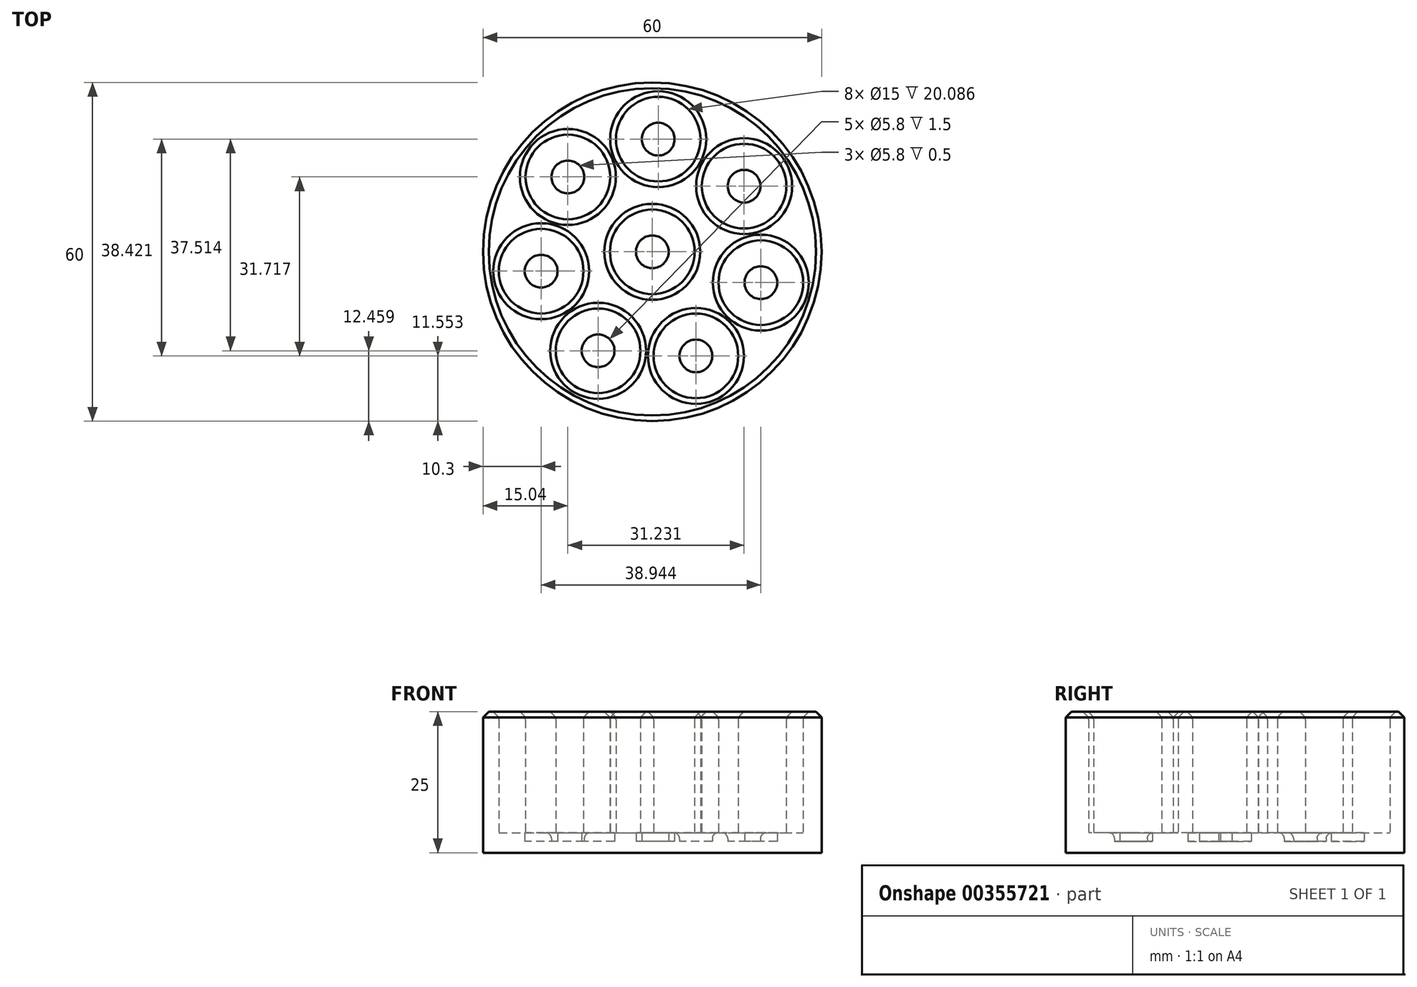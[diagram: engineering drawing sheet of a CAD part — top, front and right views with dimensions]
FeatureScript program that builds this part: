
annotation { "Feature Type Name" : "Feature", "Feature Type Description" : "" }
export const myFeature = defineFeature(function(context is Context, id is Id, definition is map)
    precondition{}
    {
        {
            var Q0;
            Q0=qCreatedBy(makeId("Top.planeOp"),FACE);
            var sketch = newSketch(context, id + "F0", { "sketchPlane" : qUnion([Q0])});
            skCircle(sketch, "E0", {"center": v(0, 0) * mm, "radius": 7.5 * mm});
            skCircle(sketch, "E1.1.0", {"center": v(-4.74, -16.7) * mm, "radius": 7.5 * mm});
            skCircle(sketch, "E1.2.0", {"center": v(5.36, -30.81) * mm, "radius": 7.5 * mm});
            skPoint(sketch, "E1.center", {"position": v(14.96, -13.27) * mm});
            skCircle(sketch, "E2.0.3.0", {"center": v(22.69, -31.72) * mm, "radius": 7.5 * mm});
            skCircle(sketch, "E2.0.4.0", {"center": v(34.2, -18.73) * mm, "radius": 7.5 * mm});
            skCircle(sketch, "E2.0.5.0", {"center": v(31.23, -1.63) * mm, "radius": 7.5 * mm});
            skCircle(sketch, "E2.0.6.0", {"center": v(16, 6.7) * mm, "radius": 7.5 * mm});
            skCircle(sketch, "E3", {"center": v(14.96, -13.27) * mm, "radius": 7.5 * mm});
            skCircle(sketch, "E4", {"center": v(14.96, -13.27) * mm, "radius": 30 * mm});
            skSolve(sketch);
        }
        {
            var Q0;
            Q0 = qSketchRegion(id + "F0", true);
            extrude(context, id + "F1", {"entities" : qUnion([Q0]), "depth" : 25 * mm});
        }
        {
            var Q0;
            Q0=makeQuery(id+"F0.imprint","IMPRINT",FACE,{"disambiguationData":[TD([[makeQuery(id+"F0.imprint","IMPRINT",EDGE,{"derivedFrom":sQuery(id+"F0.wireOp",EDGE,"E2.0.5.0")}),1.0]])]});
            var Q1;
            Q1=makeQuery(id+"F0.imprint","IMPRINT",FACE,{"disambiguationData":[TD([[makeQuery(id+"F0.imprint","IMPRINT",EDGE,{"derivedFrom":sQuery(id+"F0.wireOp",EDGE,"E2.0.4.0")}),1.0]])]});
            var Q2;
            Q2=makeQuery(id+"F0.imprint","IMPRINT",FACE,{"disambiguationData":[TD([[makeQuery(id+"F0.imprint","IMPRINT",EDGE,{"derivedFrom":sQuery(id+"F0.wireOp",EDGE,"E2.0.3.0")}),1.0]])]});
            var Q3;
            Q3=makeQuery(id+"F0.imprint","IMPRINT",FACE,{"disambiguationData":[TD([[makeQuery(id+"F0.imprint","IMPRINT",EDGE,{"derivedFrom":sQuery(id+"F0.wireOp",EDGE,"E3")}),1.0]])]});
            var Q4;
            Q4=makeQuery(id+"F0.imprint","IMPRINT",FACE,{"disambiguationData":[TD([[makeQuery(id+"F0.imprint","IMPRINT",EDGE,{"derivedFrom":sQuery(id+"F0.wireOp",EDGE,"E2.0.6.0")}),1.0]])]});
            var Q5;
            Q5=makeQuery(id+"F0.imprint","IMPRINT",FACE,{"disambiguationData":[TD([[makeQuery(id+"F0.imprint","IMPRINT",EDGE,{"derivedFrom":sQuery(id+"F0.wireOp",EDGE,"E2.0.7.0")}),1.0]])]});
            var Q6;
            Q6=makeQuery(id+"F0.imprint","IMPRINT",FACE,{"disambiguationData":[TD([[makeQuery(id+"F0.imprint","IMPRINT",EDGE,{"derivedFrom":sQuery(id+"F0.wireOp",EDGE,"E0")}),1.0]])]});
            var Q7;
            Q7=makeQuery(id+"F0.imprint","IMPRINT",FACE,{"disambiguationData":[TD([[makeQuery(id+"F0.imprint","IMPRINT",EDGE,{"derivedFrom":sQuery(id+"F0.wireOp",EDGE,"E1.2.0")}),1.0]])]});
            var Q8;
            Q8=makeQuery(id+"F0.imprint","IMPRINT",FACE,{"disambiguationData":[TD([[makeQuery(id+"F0.imprint","IMPRINT",EDGE,{"derivedFrom":sQuery(id+"F0.wireOp",EDGE,"E1.1.0")}),1.0]])]});
            extrude(context, id + "F2", {"entities" : qUnion([Q0, Q1, Q2, Q3, Q4, Q5, Q6, Q7, Q8]), "operationType" : NewBodyOperationType.ADD, "depth" : 2 * mm});
        }
        {
            var Q0;
            Q0=makeQuery(id+"F2.opExtrude","CAP_FACE",FACE,{"disambiguationData":[OSD([sQuery(id+"F0.wireOp",EDGE,"E1.1.0")])],"isStart":false});
            var sketch = newSketch(context, id + "F3", { "sketchPlane" : qUnion([Q0])});
            skPoint(sketch, "E5.0", {"position": v(-4.74, -16.7) * mm});
            skPoint(sketch, "E5.1", {"position": v(5.36, -30.81) * mm});
            skPoint(sketch, "E5.2", {"position": v(22.69, -31.72) * mm});
            skPoint(sketch, "E5.3", {"position": v(34.2, -18.73) * mm});
            skPoint(sketch, "E5.4", {"position": v(31.23, -1.63) * mm});
            skPoint(sketch, "E5.5", {"position": v(16, 6.7) * mm});
            skPoint(sketch, "E5.6", {"position": v(14.45, 7.03) * mm});
            skPoint(sketch, "E5.7", {"position": v(14.96, -13.27) * mm});
            skPoint(sketch, "E5.8", {"position": v(0, 0) * mm});
            skCircle(sketch, "E6", {"center": v(-4.74, -16.7) * mm, "radius": 2.9 * mm});
            skCircle(sketch, "E7", {"center": v(5.36, -30.81) * mm, "radius": 2.9 * mm});
            skCircle(sketch, "E8", {"center": v(22.69, -31.72) * mm, "radius": 2.9 * mm});
            skCircle(sketch, "E9", {"center": v(14.96, -13.27) * mm, "radius": 2.9 * mm});
            skCircle(sketch, "E10", {"center": v(0, 0) * mm, "radius": 2.9 * mm});
            skCircle(sketch, "E11", {"center": v(34.2, -18.73) * mm, "radius": 2.9 * mm});
            skCircle(sketch, "E12", {"center": v(31.23, -1.63) * mm, "radius": 2.9 * mm});
            skCircle(sketch, "E13", {"center": v(16, 6.7) * mm, "radius": 2.9 * mm});
            skCircle(sketch, "E14.0", {"center": v(5.36, -30.81) * mm, "radius": 7.5 * mm});
            skCircle(sketch, "E14.2", {"center": v(14.96, -13.27) * mm, "radius": 7.5 * mm});
            skCircle(sketch, "E14.3", {"center": v(22.69, -31.72) * mm, "radius": 7.5 * mm});
            skCircle(sketch, "E14.4", {"center": v(34.2, -18.73) * mm, "radius": 7.5 * mm});
            skCircle(sketch, "E14.5", {"center": v(31.23, -1.63) * mm, "radius": 7.5 * mm});
            skCircle(sketch, "E14.6", {"center": v(16, 6.7) * mm, "radius": 7.5 * mm});
            skCircle(sketch, "E14.7", {"center": v(-4.74, -16.7) * mm, "radius": 7.5 * mm});
            skCircle(sketch, "E14.8", {"center": v(0, 0) * mm, "radius": 7.5 * mm});
            skSolve(sketch);
        }
        {
            var Q0;
            Q0 = qSketchRegion(id + "F3", true);
            extrude(context, id + "F4", {"entities" : qUnion([Q0]), "operationType" : NewBodyOperationType.ADD, "depth" : 1.5 * mm});
        }
        {
            var Q0;
            Q0=makeQuery(id+"F1.opExtrude","CAP_EDGE",EDGE,{"disambiguationData":[OSD([sQuery(id+"F0.wireOp",EDGE,"E1.1.0")])],"isStart":false});
            var Q1;
            Q1=makeQuery(id+"F1.opExtrude","CAP_EDGE",EDGE,{"disambiguationData":[OSD([sQuery(id+"F0.wireOp",EDGE,"E0")])],"isStart":false});
            var Q2;
            Q2=makeQuery(id+"F1.opExtrude","CAP_EDGE",EDGE,{"disambiguationData":[OSD([sQuery(id+"F0.wireOp",EDGE,"E2.0.7.0")])],"isStart":false});
            var Q3;
            Q3=makeQuery(id+"F1.opExtrude","CAP_EDGE",EDGE,{"disambiguationData":[OSD([sQuery(id+"F0.wireOp",EDGE,"E2.0.6.0")])],"isStart":false});
            var Q4;
            Q4=makeQuery(id+"F1.opExtrude","CAP_EDGE",EDGE,{"disambiguationData":[OSD([sQuery(id+"F0.wireOp",EDGE,"E2.0.5.0")])],"isStart":false});
            var Q5;
            Q5=makeQuery(id+"F1.opExtrude","CAP_EDGE",EDGE,{"disambiguationData":[OSD([sQuery(id+"F0.wireOp",EDGE,"E2.0.4.0")])],"isStart":false});
            var Q6;
            Q6=makeQuery(id+"F1.opExtrude","CAP_EDGE",EDGE,{"disambiguationData":[OSD([sQuery(id+"F0.wireOp",EDGE,"E3")])],"isStart":false});
            var Q7;
            Q7=makeQuery(id+"F1.opExtrude","CAP_EDGE",EDGE,{"disambiguationData":[OSD([sQuery(id+"F0.wireOp",EDGE,"E1.2.0")])],"isStart":false});
            var Q8;
            Q8=makeQuery(id+"F1.opExtrude","CAP_EDGE",EDGE,{"disambiguationData":[OSD([sQuery(id+"F0.wireOp",EDGE,"E2.0.3.0")])],"isStart":false});
            var Q9;
            Q9=makeQuery(id+"F1.opExtrude","CAP_EDGE",EDGE,{"disambiguationData":[OSD([sQuery(id+"F0.wireOp",EDGE,"E4")])],"isStart":false});
            chamfer(context, id + "F5", {"entities" : qUnion([Q0, Q1, Q2, Q3, Q4, Q5, Q6, Q7, Q8, Q9]), "width" : 1 * mm, "tangentPropagation" : true});
        }
        {
            var Q0;
            {var subQ0=sQuery(id+"F0.wireOp",EDGE,"E1.2.0");Q0=makeQuery(id+"F5.opChamfer","BLEND_EDGE",EDGE,{"blendedFrom":[makeQuery(id+"F1.opExtrude","CAP_EDGE",EDGE,{"disambiguationData":[OSD([subQ0])],"isStart":false}),makeQuery(id+"F1.opExtrude","SWEPT_FACE",FACE,{"disambiguationData":[OSD([subQ0])]})],"blendedInto":[makeQuery(id+"F1.opExtrude","SWEPT_FACE",FACE,{"disambiguationData":[OSD([subQ0])]})]});}
            var Q1;
            {var subQ0=sQuery(id+"F0.wireOp",EDGE,"E1.1.0");Q1=makeQuery(id+"F5.opChamfer","BLEND_EDGE",EDGE,{"blendedFrom":[makeQuery(id+"F1.opExtrude","CAP_EDGE",EDGE,{"disambiguationData":[OSD([subQ0])],"isStart":false}),makeQuery(id+"F1.opExtrude","SWEPT_FACE",FACE,{"disambiguationData":[OSD([subQ0])]})],"blendedInto":[makeQuery(id+"F1.opExtrude","SWEPT_FACE",FACE,{"disambiguationData":[OSD([subQ0])]})]});}
            var Q2;
            {var subQ0=sQuery(id+"F0.wireOp",EDGE,"E2.0.3.0");Q2=makeQuery(id+"F5.opChamfer","BLEND_EDGE",EDGE,{"blendedFrom":[makeQuery(id+"F1.opExtrude","CAP_EDGE",EDGE,{"disambiguationData":[OSD([subQ0])],"isStart":false}),makeQuery(id+"F1.opExtrude","SWEPT_FACE",FACE,{"disambiguationData":[OSD([subQ0])]})],"blendedInto":[makeQuery(id+"F1.opExtrude","SWEPT_FACE",FACE,{"disambiguationData":[OSD([subQ0])]})]});}
            var Q3;
            {var subQ0=sQuery(id+"F0.wireOp",EDGE,"E2.0.4.0");Q3=makeQuery(id+"F5.opChamfer","BLEND_EDGE",EDGE,{"blendedFrom":[makeQuery(id+"F1.opExtrude","CAP_EDGE",EDGE,{"disambiguationData":[OSD([subQ0])],"isStart":false}),makeQuery(id+"F1.opExtrude","SWEPT_FACE",FACE,{"disambiguationData":[OSD([subQ0])]})],"blendedInto":[makeQuery(id+"F1.opExtrude","SWEPT_FACE",FACE,{"disambiguationData":[OSD([subQ0])]})]});}
            var Q4;
            {var subQ0=sQuery(id+"F0.wireOp",EDGE,"E2.0.5.0");Q4=makeQuery(id+"F5.opChamfer","BLEND_EDGE",EDGE,{"blendedFrom":[makeQuery(id+"F1.opExtrude","CAP_EDGE",EDGE,{"disambiguationData":[OSD([subQ0])],"isStart":false}),makeQuery(id+"F1.opExtrude","SWEPT_FACE",FACE,{"disambiguationData":[OSD([subQ0])]})],"blendedInto":[makeQuery(id+"F1.opExtrude","SWEPT_FACE",FACE,{"disambiguationData":[OSD([subQ0])]})]});}
            var Q5;
            {var subQ0=sQuery(id+"F0.wireOp",EDGE,"E2.0.6.0");Q5=makeQuery(id+"F5.opChamfer","BLEND_EDGE",EDGE,{"blendedFrom":[makeQuery(id+"F1.opExtrude","CAP_EDGE",EDGE,{"disambiguationData":[OSD([subQ0])],"isStart":false}),makeQuery(id+"F1.opExtrude","SWEPT_FACE",FACE,{"disambiguationData":[OSD([subQ0])]})],"blendedInto":[makeQuery(id+"F1.opExtrude","SWEPT_FACE",FACE,{"disambiguationData":[OSD([subQ0])]})]});}
            var Q6;
            {var subQ0=sQuery(id+"F0.wireOp",EDGE,"E0");Q6=makeQuery(id+"F5.opChamfer","BLEND_EDGE",EDGE,{"blendedFrom":[makeQuery(id+"F1.opExtrude","CAP_EDGE",EDGE,{"disambiguationData":[OSD([subQ0])],"isStart":false}),makeQuery(id+"F1.opExtrude","SWEPT_FACE",FACE,{"disambiguationData":[OSD([subQ0])]})],"blendedInto":[makeQuery(id+"F1.opExtrude","SWEPT_FACE",FACE,{"disambiguationData":[OSD([subQ0])]})]});}
            var Q7;
            {var subQ0=sQuery(id+"F0.wireOp",EDGE,"E3");Q7=makeQuery(id+"F5.opChamfer","BLEND_EDGE",EDGE,{"blendedFrom":[makeQuery(id+"F1.opExtrude","CAP_EDGE",EDGE,{"disambiguationData":[OSD([subQ0])],"isStart":false}),makeQuery(id+"F1.opExtrude","SWEPT_FACE",FACE,{"disambiguationData":[OSD([subQ0])]})],"blendedInto":[makeQuery(id+"F1.opExtrude","SWEPT_FACE",FACE,{"disambiguationData":[OSD([subQ0])]})]});}
            var Q8;
            Q8=makeQuery(id+"F4.opExtrude","CAP_EDGE",EDGE,{"disambiguationData":[OSD([sQuery(id+"F3.wireOp",EDGE,"E7")])],"isStart":true});
            var Q9;
            Q9=makeQuery(id+"F4.opExtrude","CAP_EDGE",EDGE,{"disambiguationData":[OSD([sQuery(id+"F3.wireOp",EDGE,"E6")])],"isStart":true});
            var Q10;
            Q10=makeQuery(id+"F4.opExtrude","CAP_EDGE",EDGE,{"disambiguationData":[OSD([sQuery(id+"F3.wireOp",EDGE,"E10")])],"isStart":false});
            var Q11;
            Q11=makeQuery(id+"F4.opExtrude","CAP_EDGE",EDGE,{"disambiguationData":[OSD([sQuery(id+"F3.wireOp",EDGE,"Eor7ybkG-s9XB-PS9b-kSbm-frpLWbX5gBem")])],"isStart":true});
            var Q12;
            Q12=makeQuery(id+"F4.opExtrude","CAP_EDGE",EDGE,{"disambiguationData":[OSD([sQuery(id+"F3.wireOp",EDGE,"E9")])],"isStart":true});
            var Q13;
            Q13=makeQuery(id+"F4.opExtrude","CAP_EDGE",EDGE,{"disambiguationData":[OSD([sQuery(id+"F3.wireOp",EDGE,"E8")])],"isStart":false});
            var Q14;
            Q14=makeQuery(id+"F4.opExtrude","CAP_EDGE",EDGE,{"disambiguationData":[OSD([sQuery(id+"F3.wireOp",EDGE,"E11")])],"isStart":true});
            var Q15;
            Q15=makeQuery(id+"F4.opExtrude","CAP_EDGE",EDGE,{"disambiguationData":[OSD([sQuery(id+"F3.wireOp",EDGE,"E12")])],"isStart":false});
            var Q16;
            Q16=makeQuery(id+"F4.opExtrude","CAP_EDGE",EDGE,{"disambiguationData":[OSD([sQuery(id+"F3.wireOp",EDGE,"E13")])],"isStart":true});
            var Q17;
            Q17=makeQuery(id+"F4.opExtrude","CAP_EDGE",EDGE,{"disambiguationData":[OSD([sQuery(id+"F3.wireOp",EDGE,"E14.6")])],"isStart":false});
            var Q18;
            Q18=makeQuery(id+"F4.opExtrude","CAP_EDGE",EDGE,{"disambiguationData":[OSD([sQuery(id+"F3.wireOp",EDGE,"E14.2")])],"isStart":false});
            var Q19;
            Q19=makeQuery(id+"F4.opExtrude","CAP_EDGE",EDGE,{"disambiguationData":[OSD([sQuery(id+"F3.wireOp",EDGE,"E14.1")])],"isStart":false});
            var Q20;
            Q20=makeQuery(id+"F4.opExtrude","CAP_EDGE",EDGE,{"disambiguationData":[OSD([sQuery(id+"F3.wireOp",EDGE,"E14.8")])],"isStart":false});
            var Q21;
            Q21=makeQuery(id+"F4.opExtrude","CAP_EDGE",EDGE,{"disambiguationData":[OSD([sQuery(id+"F3.wireOp",EDGE,"E14.7")])],"isStart":false});
            var Q22;
            Q22=makeQuery(id+"F4.opExtrude","CAP_EDGE",EDGE,{"disambiguationData":[OSD([sQuery(id+"F3.wireOp",EDGE,"E14.0")])],"isStart":false});
            var Q23;
            Q23=makeQuery(id+"F4.opExtrude","CAP_EDGE",EDGE,{"disambiguationData":[OSD([sQuery(id+"F3.wireOp",EDGE,"E14.3")])],"isStart":false});
            var Q24;
            Q24=makeQuery(id+"F4.opExtrude","CAP_EDGE",EDGE,{"disambiguationData":[OSD([sQuery(id+"F3.wireOp",EDGE,"E14.4")])],"isStart":false});
            var Q25;
            Q25=makeQuery(id+"F4.opExtrude","CAP_EDGE",EDGE,{"disambiguationData":[OSD([sQuery(id+"F3.wireOp",EDGE,"E14.5")])],"isStart":false});
            fillet(context, id + "F6", {"entities" : qUnion([Q0, Q1, Q2, Q3, Q4, Q5, Q6, Q7, Q8, Q9, Q10, Q11, Q12, Q13, Q14, Q15, Q16, Q17, Q18, Q19, Q20, Q21, Q22, Q23, Q24, Q25]), "radius" : 1 * mm, "tangentPropagation" : true, "allowEdgeOverflow" : false});
        }
    });
